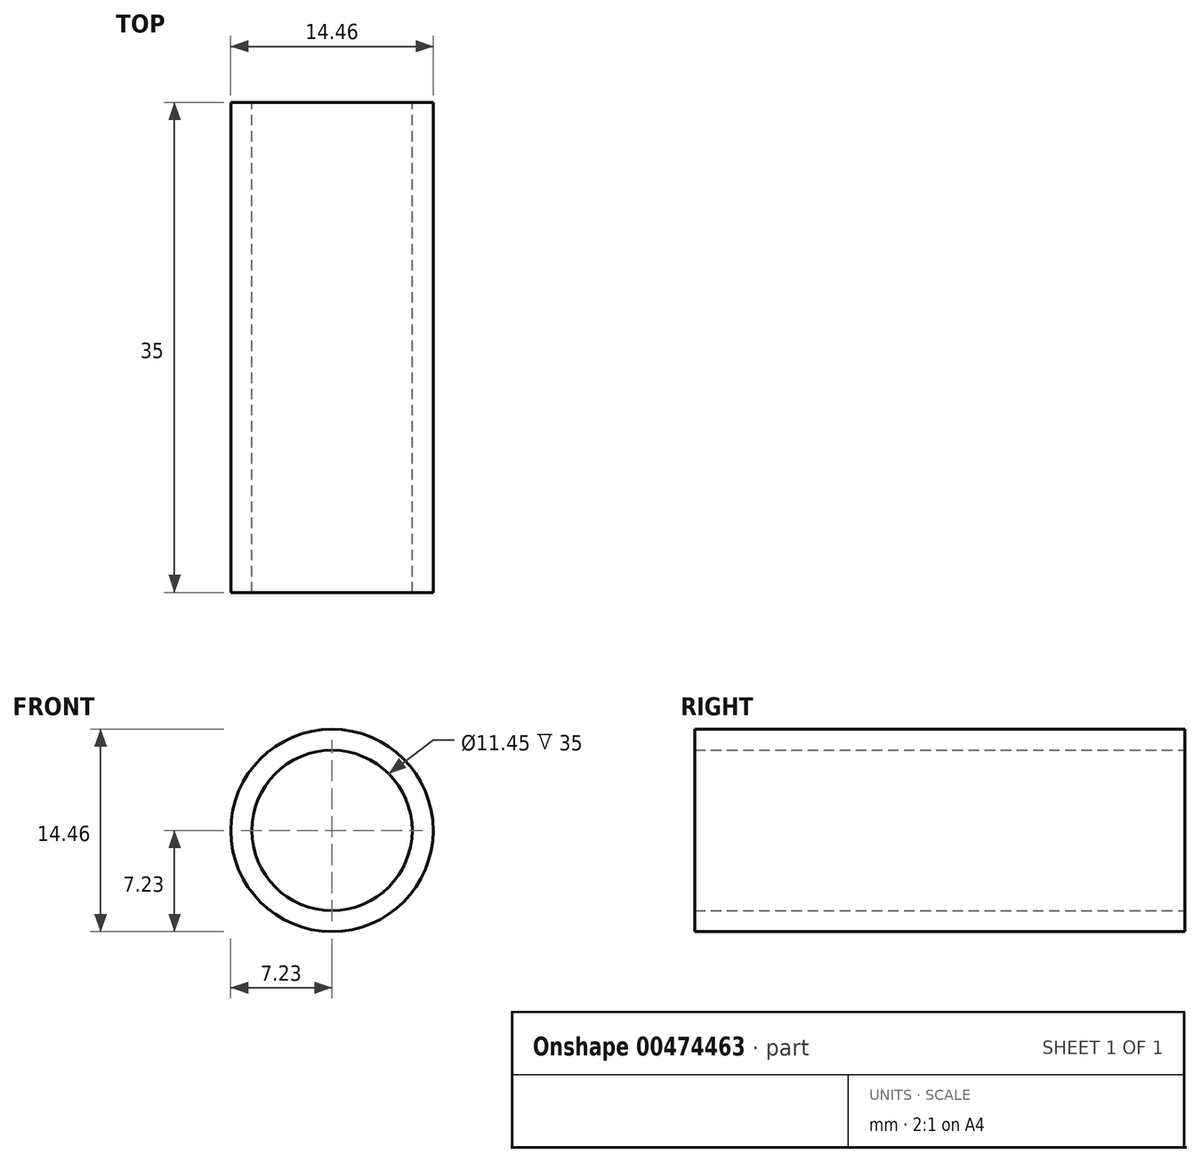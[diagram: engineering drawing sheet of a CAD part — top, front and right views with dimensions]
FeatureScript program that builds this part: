
annotation { "Feature Type Name" : "Feature", "Feature Type Description" : "" }
export const myFeature = defineFeature(function(context is Context, id is Id, definition is map)
    precondition{}
    {
        {
            var Q0;
            Q0=qCreatedBy(makeId("Front.planeOp"),FACE);
            var sketch = newSketch(context, id + "F0", { "sketchPlane" : qUnion([Q0])});
            skCircle(sketch, "E0", {"center": v(0, 0) * mm, "radius": 5.72 * mm});
            skCircle(sketch, "E1", {"center": v(0, 0) * mm, "radius": 7.23 * mm});
            skSolve(sketch);
        }
        {
            var Q0;
            Q0=makeQuery(id+"F0.imprint","IMPRINT",FACE,{"disambiguationData":[TD([[makeQuery(id+"F0.imprint","IMPRINT",EDGE,{"derivedFrom":sQuery(id+"F0.wireOp",EDGE,"E0")}),-1.0]])]});
            extrude(context, id + "F1", {"entities" : qUnion([Q0]), "depth" : 35 * mm});
        }
    });
